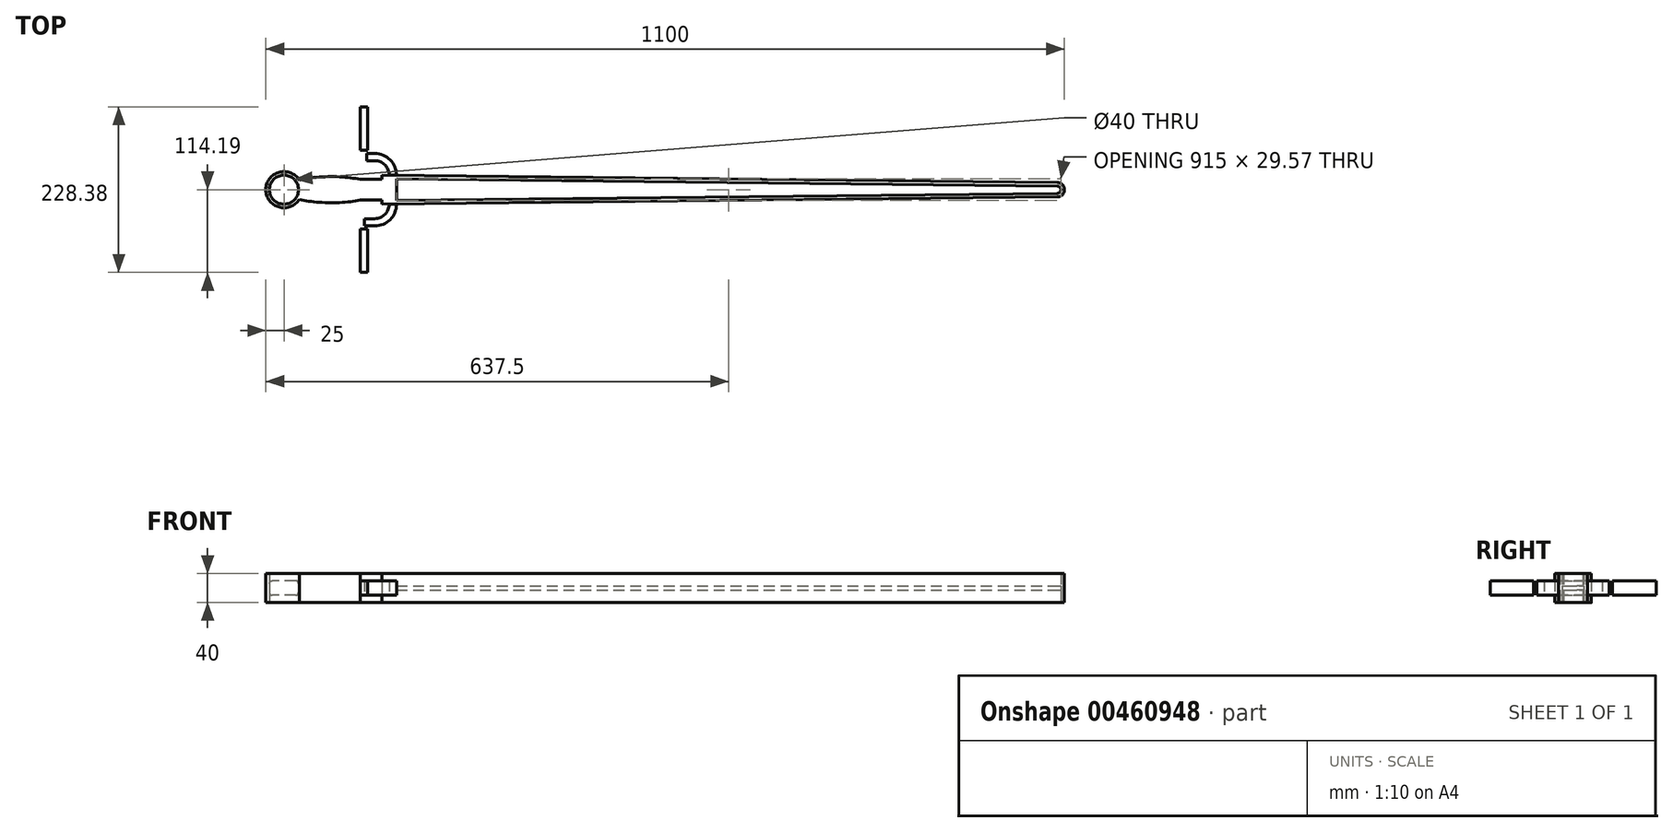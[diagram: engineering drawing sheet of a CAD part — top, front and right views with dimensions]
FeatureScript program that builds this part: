
annotation { "Feature Type Name" : "Feature", "Feature Type Description" : "" }
export const myFeature = defineFeature(function(context is Context, id is Id, definition is map)
    precondition{}
    {
        {
            var Q0;
            Q0=qCreatedBy(makeId("Top.planeOp"),FACE);
            var sketch = newSketch(context, id + "F0", { "sketchPlane" : qUnion([Q0])});
            skArc(sketch, "E0", {"start": v(-20, 0) * mm, "mid": v(0, 20) * mm, "end": v(20, 0) * mm});
            skArc(sketch, "E1.0", {"start": v(-25, 0) * mm, "mid": v(-6.92, 24.02) * mm, "end": v(21.17, 13.3) * mm});
            skLineSegment(sketch, "E2", {"start": v(-25, 0) * mm, "end": v(1075, 0) * mm, "construction": true});
            skPoint(sketch, "E3", {"position": v(65, 0) * mm});
            skPoint(sketch, "E4", {"position": v(25, 0) * mm});
            skLineSegment(sketch, "E5", {"start": v(65, 0) * mm, "end": v(65, 18) * mm, "construction": true});
            skEllipticalArc(sketch, "E6", {});
            skPoint(sketch, "E7", {"position": v(105, 0) * mm});
            skLineSegment(sketch, "E8", {"start": v(105, 0) * mm, "end": v(105, 14.19) * mm, "construction": true});
            skPoint(sketch, "E9", {"position": v(1065, 0) * mm});
            skArc(sketch, "E10", {"start": v(1075, 0) * mm, "mid": v(1072.1, 7.03) * mm, "end": v(1065.1, 10) * mm});
            skPoint(sketch, "E11", {"position": v(135, 0) * mm});
            skPoint(sketch, "E12", {"position": v(145, 0) * mm});
            skLineSegment(sketch, "E13", {"start": v(135, 0) * mm, "end": v(135, 20) * mm, "construction": true});
            skLineSegment(sketch, "E14", {"start": v(135, 20) * mm, "end": v(1065.1, 10) * mm});
            skLineSegment(sketch, "E15", {"start": v(105, 14.19) * mm, "end": v(135, 14.19) * mm});
            skArc(sketch, "E16", {"start": v(21.17, 13.3) * mm, "mid": v(24.02, 6.92) * mm, "end": v(25, 0) * mm, "construction": true});
            skLineSegment(sketch, "E17", {"start": v(135, 14.19) * mm, "end": v(135, 20) * mm});
            skArc(sketch, "E18.MirrorCS", {"start": v(-20, 0) * mm, "mid": v(0, -20) * mm, "end": v(20, 0) * mm});
            skArc(sketch, "E19.MirrorCS", {"start": v(-25, 0) * mm, "mid": v(-6.92, -24.02) * mm, "end": v(21.17, -13.3) * mm});
            skEllipticalArc(sketch, "E20.MirrorCS", {});
            skLineSegment(sketch, "E21.MirrorCS", {"start": v(105, -14.19) * mm, "end": v(135, -14.19) * mm});
            skLineSegment(sketch, "E22.MirrorCS", {"start": v(135, -14.19) * mm, "end": v(135, -20) * mm});
            skLineSegment(sketch, "E23.MirrorCS", {"start": v(135, -20) * mm, "end": v(1065.1, -10) * mm});
            skArc(sketch, "E24.MirrorCS", {"start": v(1075, 0) * mm, "mid": v(1072.1, -7.03) * mm, "end": v(1065.1, -10) * mm});
            skPoint(sketch, "E25", {"position": v(155, 0) * mm});
            skPoint(sketch, "E26", {"position": v(1070, 0) * mm});
            skLineSegment(sketch, "E27.1", {"start": v(155, -14.78) * mm, "end": v(1065.05, -5) * mm});
            skLineSegment(sketch, "E27.3", {"start": v(155, 14.78) * mm, "end": v(1065.05, 5) * mm});
            skArc(sketch, "E27.4", {"start": v(1070, 0) * mm, "mid": v(1068.55, 3.52) * mm, "end": v(1065.05, 5) * mm});
            skArc(sketch, "E27.5", {"start": v(1070, 0) * mm, "mid": v(1068.55, -3.52) * mm, "end": v(1065.05, -5) * mm});
            skLineSegment(sketch, "E28", {"start": v(155, 0) * mm, "end": v(155, 14.78) * mm});
            skLineSegment(sketch, "E29.MirrorCS", {"start": v(155, 0) * mm, "end": v(155, -14.78) * mm});
            const initialGuessF0  = {"E6": [0.06500000014901161, 0, -1, 0, 0.06500000014901161, 0.018, 4.04951515852442, 5.452351675529847], "E20.MirrorCS": [0.06500000014901161, 0, -1, 0, 0.06500000014901161, 0.018, 0.8308336316497391, 2.233670148655166]};
            skSetInitialGuess(sketch, initialGuessF0);
            skSolve(sketch);
        }
        {
            var Q0;
            Q0=sQuery(id+"F0.wireOp",EDGE,"E8");
            cPlane(context, id + "F1", {"entities" : qUnion([Q0]), "cplaneType" : CPlaneType.LINE_ANGLE, "offset" : 25 * mm, "angle" : 90 * degree, "width" : 150 * mm, "height" : 150 * mm});
        }
        {
            var Q0;
            Q0=makeQuery(id+"F0.imprint","IMPRINT",FACE,{"disambiguationData":[TD([[makeQuery(id+"F0.imprint","IMPRINT",EDGE,{"derivedFrom":sQuery(id+"F0.wireOp",EDGE,"E0")}),1.0]])]});
            extrude(context, id + "F2", {"entities" : qUnion([Q0]), "endBound" : BoundingType.SYMMETRIC, "depth" : 20 * mm});
        }
        {
            var Q0;
            Q0=makeQuery(id+"F0.imprint","IMPRINT",FACE,{"disambiguationData":[TD([[makeQuery(id+"F0.imprint","IMPRINT",EDGE,{"derivedFrom":sQuery(id+"F0.wireOp",EDGE,"E27.1")}),1.0]])]});
            extrude(context, id + "F3", {"entities" : qUnion([Q0]), "operationType" : NewBodyOperationType.ADD, "endBound" : BoundingType.SYMMETRIC, "depth" : 6 * mm});
        }
        {
            var Q0;
            Q0=makeQuery(id+"F0.imprint","IMPRINT",FACE,{"disambiguationData":[TD([[makeQuery(id+"F0.imprint","IMPRINT",EDGE,{"derivedFrom":sQuery(id+"F0.wireOp",EDGE,"E0")}),-1.0]])]});
            extrude(context, id + "F4", {"entities" : qUnion([Q0]), "endBound" : BoundingType.SYMMETRIC, "depth" : 40 * mm});
        }
        {
            var Q0;
            Q0=qCreatedBy(id+"F1.planeOp",FACE);
            var sketch = newSketch(context, id + "F5", { "sketchPlane" : qUnion([Q0])});
            skLineSegment(sketch, "E30.0.1", {"start": v(14.19, -10) * mm, "end": v(14.19, 10) * mm});
            skLineSegment(sketch, "E30.0.3", {"start": v(14.19, 10) * mm, "end": v(14.19, -10) * mm});
            skLineSegment(sketch, "E31.0.1", {"start": v(-14.19, -10) * mm, "end": v(-14.19, 10) * mm});
            skLineSegment(sketch, "E31.0.3", {"start": v(-14.19, 10) * mm, "end": v(-14.19, -10) * mm});
            skLineSegment(sketch, "E32", {"start": v(14.19, -10) * mm, "end": v(-14.19, -10) * mm});
            skLineSegment(sketch, "E33", {"start": v(-14.19, 10) * mm, "end": v(14.19, 10) * mm});
            skLineSegment(sketch, "E34", {"start": v(14.19, 10) * mm, "end": v(114.19, 10) * mm});
            skLineSegment(sketch, "E35", {"start": v(14.19, -10) * mm, "end": v(114.19, -10) * mm});
            skLineSegment(sketch, "E36", {"start": v(114.19, -10) * mm, "end": v(114.19, 10) * mm});
            skLineSegment(sketch, "E37", {"start": v(0, -10) * mm, "end": v(0, 10) * mm, "construction": true});
            skLineSegment(sketch, "E38.MirrorCS", {"start": v(-14.19, -10) * mm, "end": v(-114.19, -10) * mm});
            skLineSegment(sketch, "E39.MirrorCS", {"start": v(-14.19, 10) * mm, "end": v(-114.19, 10) * mm});
            skLineSegment(sketch, "E40.MirrorCS", {"start": v(-114.19, -10) * mm, "end": v(-114.19, 10) * mm});
            skPoint(sketch, "E41", {"position": v(-64.19, 10) * mm});
            skLineSegment(sketch, "E42", {"start": v(-64.19, 10) * mm, "end": v(-64.19, -10) * mm});
            skLineSegment(sketch, "E43.MirrorCS", {"start": v(64.19, 10) * mm, "end": v(64.19, -10) * mm});
            skLineSegment(sketch, "E44.0", {"start": v(-54.19, 10) * mm, "end": v(-54.19, -10) * mm});
            skLineSegment(sketch, "E45.MirrorCS", {"start": v(54.19, 10) * mm, "end": v(54.19, -10) * mm});
            skSolve(sketch);
        }
        {
            var Q0;
            {var subQ0=sQuery(id+"F5.wireOp",EDGE,"E40.MirrorCS");Q0=makeQuery(id+"F5.imprint","IMPRINT",FACE,{"disambiguationData":[TD([[makeQuery(id+"F5.imprint","IMPRINT",EDGE,{"derivedFrom":subQ0}),-1.0]])]});}
            var Q1;
            {var subQ0=sQuery(id+"F5.wireOp",EDGE,"E42");Q1=makeQuery(id+"F5.imprint","IMPRINT",FACE,{"disambiguationData":[TD([[makeQuery(id+"F5.imprint","IMPRINT",EDGE,{"derivedFrom":subQ0}),1.0]])]});}
            var Q2;
            {var subQ0=sQuery(id+"F5.wireOp",EDGE,"E31.0.3");Q2=makeQuery(id+"F5.imprint","IMPRINT",FACE,{"disambiguationData":[TD([[makeQuery(id+"F5.imprint","IMPRINT",EDGE,{"derivedFrom":subQ0}),-1.0]])]});}
            var Q3;
            {var subQ0=sQuery(id+"F5.wireOp",EDGE,"E30.0.3");Q3=makeQuery(id+"F5.imprint","IMPRINT",FACE,{"disambiguationData":[TD([[makeQuery(id+"F5.imprint","IMPRINT",EDGE,{"derivedFrom":subQ0}),1.0]])]});}
            var Q4;
            {var subQ0=sQuery(id+"F5.wireOp",EDGE,"E43.MirrorCS");Q4=makeQuery(id+"F5.imprint","IMPRINT",FACE,{"disambiguationData":[TD([[makeQuery(id+"F5.imprint","IMPRINT",EDGE,{"derivedFrom":subQ0}),-1.0]])]});}
            var Q5;
            {var subQ0=sQuery(id+"F5.wireOp",EDGE,"E36");Q5=makeQuery(id+"F5.imprint","IMPRINT",FACE,{"disambiguationData":[TD([[makeQuery(id+"F5.imprint","IMPRINT",EDGE,{"derivedFrom":subQ0}),1.0]])]});}
            extrude(context, id + "F6", {"entities" : qUnion([Q0, Q1, Q2, Q3, Q4, Q5]), "depth" : 10 * mm});
        }
        {
            var Q0;
            Q0=qCreatedBy(id+"F1.planeOp",FACE);
            cPlane(context, id + "F7", {"entities" : qUnion([Q0]), "cplaneType" : CPlaneType.OFFSET, "offset" : 20 * mm, "width" : 150 * mm, "height" : 150 * mm});
        }
        {
            var Q0;
            Q0=qCreatedBy(id+"F7.planeOp",FACE);
            var sketch = newSketch(context, id + "F8", { "sketchPlane" : qUnion([Q0])});
            skLineSegment(sketch, "E46.0", {"start": v(20, 10) * mm, "end": v(20, -10) * mm});
            skLineSegment(sketch, "E47.0", {"start": v(-20, 10) * mm, "end": v(-20, -10) * mm});
            skLineSegment(sketch, "E48", {"start": v(20, 10) * mm, "end": v(40, 10) * mm, "construction": true});
            skLineSegment(sketch, "E49.bottom", {"start": v(40, 10) * mm, "end": v(50, 10) * mm});
            skLineSegment(sketch, "E49.top", {"start": v(40, -10) * mm, "end": v(50, -10) * mm});
            skLineSegment(sketch, "E49.left", {"start": v(40, 10) * mm, "end": v(40, -10) * mm});
            skLineSegment(sketch, "E49.right", {"start": v(50, 10) * mm, "end": v(50, -10) * mm});
            skLineSegment(sketch, "E50", {"start": v(-20, 10) * mm, "end": v(-40, 10) * mm, "construction": true});
            skLineSegment(sketch, "E51.bottom", {"start": v(-40, 10) * mm, "end": v(-50, 10) * mm});
            skLineSegment(sketch, "E51.top", {"start": v(-40, -10) * mm, "end": v(-50, -10) * mm});
            skLineSegment(sketch, "E51.left", {"start": v(-40, 10) * mm, "end": v(-40, -10) * mm});
            skLineSegment(sketch, "E51.right", {"start": v(-50, 10) * mm, "end": v(-50, -10) * mm});
            skSolve(sketch);
        }
        {
            var Q0;
            Q0=makeQuery(id+"F8.imprint","IMPRINT",FACE,{"disambiguationData":[TD([[makeQuery(id+"F8.imprint","IMPRINT",EDGE,{"derivedFrom":sQuery(id+"F8.wireOp",EDGE,"E49.bottom")}),-1.0]])]});
            var Q1;
            Q1=sQuery(id+"F8.wireOp",EDGE,"E46.0");
            revolve(context, id + "F9", {"entities" : qUnion([Q0]), "axis" : qUnion([Q1]), "revolveType" : RevolveType.ONE_DIRECTION, "angle" : 90 * degree});
        }
        {
            var Q0;
            Q0=makeQuery(id+"F8.imprint","IMPRINT",FACE,{"disambiguationData":[TD([[makeQuery(id+"F8.imprint","IMPRINT",EDGE,{"derivedFrom":sQuery(id+"F8.wireOp",EDGE,"E51.bottom")}),1.0]])]});
            var Q1;
            Q1=sQuery(id+"F8.wireOp",EDGE,"E47.0");
            revolve(context, id + "F10", {"entities" : qUnion([Q0]), "axis" : qUnion([Q1]), "revolveType" : RevolveType.ONE_DIRECTION, "oppositeDirection" : true, "angle" : 90 * degree});
        }
        {
            var Q0;
            Q0=makeQuery(id+"F8.imprint","IMPRINT",FACE,{"disambiguationData":[TD([[makeQuery(id+"F8.imprint","IMPRINT",EDGE,{"derivedFrom":sQuery(id+"F8.wireOp",EDGE,"E49.bottom")}),-1.0]])]});
            extrude(context, id + "F11", {"entities" : qUnion([Q0]), "operationType" : NewBodyOperationType.ADD, "oppositeDirection" : true, "depth" : 11.1 * mm});
        }
        {
            var Q0;
            Q0=makeQuery(id+"F8.imprint","IMPRINT",FACE,{"disambiguationData":[TD([[makeQuery(id+"F8.imprint","IMPRINT",EDGE,{"derivedFrom":sQuery(id+"F8.wireOp",EDGE,"E51.bottom")}),1.0]])]});
            extrude(context, id + "F12", {"entities" : qUnion([Q0]), "operationType" : NewBodyOperationType.ADD, "oppositeDirection" : true, "depth" : 14.4 * mm});
        }
        {
            var Q0;
            Q0=makeQuery(id+"F2.opExtrude","CAP_EDGE",EDGE,{"disambiguationData":[OSD([sQuery(id+"F0.wireOp",EDGE,"E1.0"),sQuery(id+"F0.wireOp",EDGE,"E19.MirrorCS")])],"isStart":false});
            var Q1;
            Q1=makeQuery(id+"F2.opExtrude","CAP_EDGE",EDGE,{"disambiguationData":[OSD([sQuery(id+"F0.wireOp",EDGE,"E6")])],"isStart":false});
            var Q2;
            Q2=makeQuery(id+"F2.opExtrude","CAP_EDGE",EDGE,{"disambiguationData":[OSD([sQuery(id+"F0.wireOp",EDGE,"E20.MirrorCS")])],"isStart":false});
            var Q3;
            Q3=makeQuery(id+"F2.opExtrude","CAP_EDGE",EDGE,{"disambiguationData":[OSD([sQuery(id+"F0.wireOp",EDGE,"E1.0"),sQuery(id+"F0.wireOp",EDGE,"E19.MirrorCS")])],"isStart":true});
            var Q4;
            Q4=makeQuery(id+"F2.opExtrude","CAP_EDGE",EDGE,{"disambiguationData":[OSD([sQuery(id+"F0.wireOp",EDGE,"E6")])],"isStart":true});
            var Q5;
            Q5=makeQuery(id+"F2.opExtrude","CAP_EDGE",EDGE,{"disambiguationData":[OSD([sQuery(id+"F0.wireOp",EDGE,"E20.MirrorCS")])],"isStart":true});
            var Q6;
            Q6=makeQuery(id+"F2.opExtrude","CAP_EDGE",EDGE,{"disambiguationData":[OSD([sQuery(id+"F0.wireOp",EDGE,"E21.MirrorCS")])],"isStart":true});
            var Q7;
            Q7=makeQuery(id+"F2.opExtrude","CAP_EDGE",EDGE,{"disambiguationData":[OSD([sQuery(id+"F0.wireOp",EDGE,"E15")])],"isStart":true});
            var Q8;
            Q8=makeQuery(id+"F2.opExtrude","CAP_FACE",FACE,{"disambiguationData":[OSD([sQuery(id+"F0.wireOp",EDGE,"E0"),sQuery(id+"F0.wireOp",EDGE,"E1.0"),sQuery(id+"F0.wireOp",EDGE,"E6"),sQuery(id+"F0.wireOp",EDGE,"E10"),sQuery(id+"F0.wireOp",EDGE,"E14"),sQuery(id+"F0.wireOp",EDGE,"E15"),sQuery(id+"F0.wireOp",EDGE,"E17"),sQuery(id+"F0.wireOp",EDGE,"E18.MirrorCS"),sQuery(id+"F0.wireOp",EDGE,"E19.MirrorCS"),sQuery(id+"F0.wireOp",EDGE,"E20.MirrorCS"),sQuery(id+"F0.wireOp",EDGE,"E21.MirrorCS"),sQuery(id+"F0.wireOp",EDGE,"E22.MirrorCS"),sQuery(id+"F0.wireOp",EDGE,"E23.MirrorCS"),sQuery(id+"F0.wireOp",EDGE,"E24.MirrorCS"),sQuery(id+"F0.wireOp",EDGE,"E27.1"),sQuery(id+"F0.wireOp",EDGE,"E27.3"),sQuery(id+"F0.wireOp",EDGE,"E27.4"),sQuery(id+"F0.wireOp",EDGE,"E27.5"),sQuery(id+"F0.wireOp",EDGE,"E28"),sQuery(id+"F0.wireOp",EDGE,"E29.MirrorCS")])],"isStart":false});
            var Q9;
            Q9=makeQuery(id+"F2.opExtrude","CAP_FACE",FACE,{"disambiguationData":[OSD([sQuery(id+"F0.wireOp",EDGE,"E0"),sQuery(id+"F0.wireOp",EDGE,"E1.0"),sQuery(id+"F0.wireOp",EDGE,"E6"),sQuery(id+"F0.wireOp",EDGE,"E10"),sQuery(id+"F0.wireOp",EDGE,"E14"),sQuery(id+"F0.wireOp",EDGE,"E15"),sQuery(id+"F0.wireOp",EDGE,"E17"),sQuery(id+"F0.wireOp",EDGE,"E18.MirrorCS"),sQuery(id+"F0.wireOp",EDGE,"E19.MirrorCS"),sQuery(id+"F0.wireOp",EDGE,"E20.MirrorCS"),sQuery(id+"F0.wireOp",EDGE,"E21.MirrorCS"),sQuery(id+"F0.wireOp",EDGE,"E22.MirrorCS"),sQuery(id+"F0.wireOp",EDGE,"E23.MirrorCS"),sQuery(id+"F0.wireOp",EDGE,"E24.MirrorCS"),sQuery(id+"F0.wireOp",EDGE,"E27.1"),sQuery(id+"F0.wireOp",EDGE,"E27.3"),sQuery(id+"F0.wireOp",EDGE,"E27.4"),sQuery(id+"F0.wireOp",EDGE,"E27.5"),sQuery(id+"F0.wireOp",EDGE,"E28"),sQuery(id+"F0.wireOp",EDGE,"E29.MirrorCS")])],"isStart":true});
            fillet(context, id + "F13", {"entities" : qUnion([Q0, Q1, Q2, Q3, Q4, Q5, Q6, Q7, Q8, Q9]), "radius" : 3.8 * mm, "tangentPropagation" : true, "allowEdgeOverflow" : false});
        }
    });
